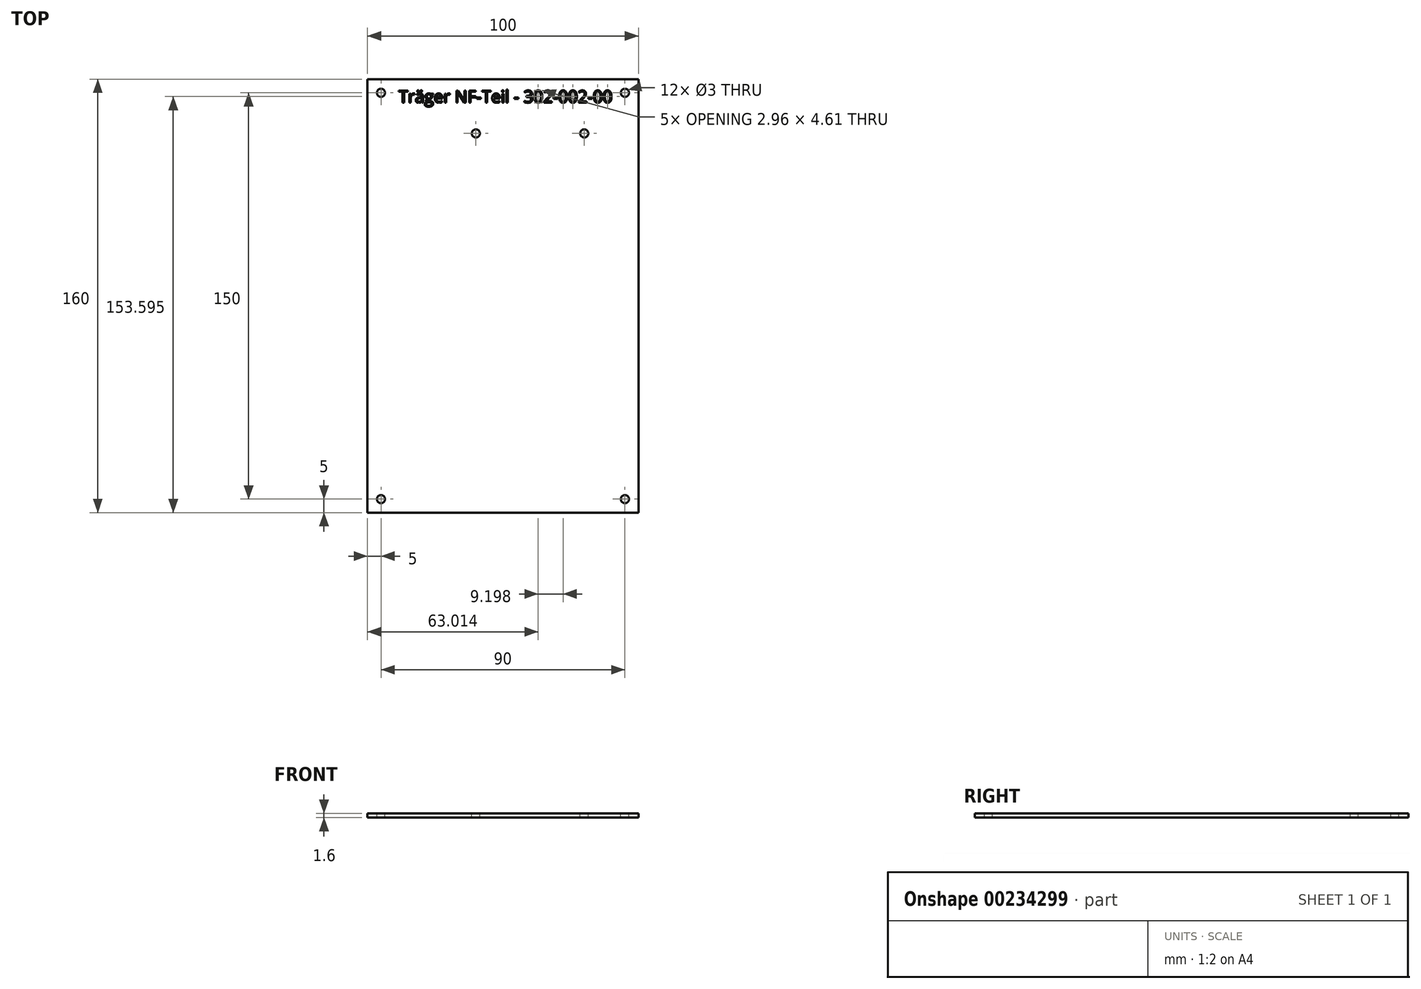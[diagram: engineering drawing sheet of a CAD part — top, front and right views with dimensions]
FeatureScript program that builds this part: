
annotation { "Feature Type Name" : "Feature", "Feature Type Description" : "" }
export const myFeature = defineFeature(function(context is Context, id is Id, definition is map)
    precondition{}
    {
        {
            var Q0;
            Q0=qCreatedBy(makeId("Top.planeOp"),FACE);
            var sketch = newSketch(context, id + "F0", { "sketchPlane" : qUnion([Q0])});
            skLineSegment(sketch, "E0.bottom", {"start": v(50, -80) * mm, "end": v(-50, -80) * mm});
            skLineSegment(sketch, "E0.top", {"start": v(50, 80) * mm, "end": v(-50, 80) * mm});
            skLineSegment(sketch, "E0.left", {"start": v(50, -80) * mm, "end": v(50, 80) * mm});
            skLineSegment(sketch, "E0.right", {"start": v(-50, -80) * mm, "end": v(-50, 80) * mm});
            skPoint(sketch, "E0.middle", {"position": v(0, 0) * mm});
            skCircle(sketch, "E1", {"center": v(-45, 75) * mm, "radius": 1.5 * mm});
            skCircle(sketch, "E2.MirrorC", {"center": v(45, 75) * mm, "radius": 1.5 * mm});
            skCircle(sketch, "E3.MirrorC", {"center": v(-45, -75) * mm, "radius": 1.5 * mm});
            skCircle(sketch, "E4.MirrorC", {"center": v(45, -75) * mm, "radius": 1.5 * mm});
            skCircle(sketch, "E5", {"center": v(-10, 60) * mm, "radius": 1.5 * mm});
            skCircle(sketch, "E6", {"center": v(30, 60) * mm, "radius": 1.5 * mm});
            skSolve(sketch);
        }
        {
            var Q0;
            Q0=makeQuery(id+"F0.imprint","IMPRINT",FACE,{"disambiguationData":[TD([[makeQuery(id+"F0.imprint","IMPRINT",EDGE,{"derivedFrom":sQuery(id+"F0.wireOp",EDGE,"E0.bottom")}),-1.0]])]});
            extrude(context, id + "F1", {"entities" : qUnion([Q0]), "oppositeDirection" : true, "depth" : 1.6 * mm});
        }
        {
            var Q0;
            Q0=makeQuery(id+"F1.opExtrude","CAP_FACE",FACE,{"disambiguationData":[OSD([sQuery(id+"F0.wireOp",EDGE,"E0.bottom"),sQuery(id+"F0.wireOp",EDGE,"E0.top"),sQuery(id+"F0.wireOp",EDGE,"E0.left"),sQuery(id+"F0.wireOp",EDGE,"E0.right"),sQuery(id+"F0.wireOp",EDGE,"E1"),sQuery(id+"F0.wireOp",EDGE,"E2.MirrorC"),sQuery(id+"F0.wireOp",EDGE,"E3.MirrorC"),sQuery(id+"F0.wireOp",EDGE,"E4.MirrorC"),sQuery(id+"F0.wireOp",EDGE,"E5"),sQuery(id+"F0.wireOp",EDGE,"E6")])],"isStart":true});
            var sketch = newSketch(context, id + "F2", { "sketchPlane" : qUnion([Q0])});
            skText(sketch, "E7", { "text": "Träger NF-Teil - 302-002-00", "fontName": "OpenSans-Regular.ttf"});
            const initialGuessF2  = {"E7": [-0.0385, 0.07135, 1, 0, 0.00452]};
            skSetInitialGuess(sketch, initialGuessF2);
            skSolve(sketch);
        }
        {
            var Q0;
            Q0 = qSketchRegion(id + "F2", true);
            extrude(context, id + "F3", {"entities" : qUnion([Q0]), "operationType" : NewBodyOperationType.REMOVE, "oppositeDirection" : true, "depth" : .1 * mm});
        }
    });
